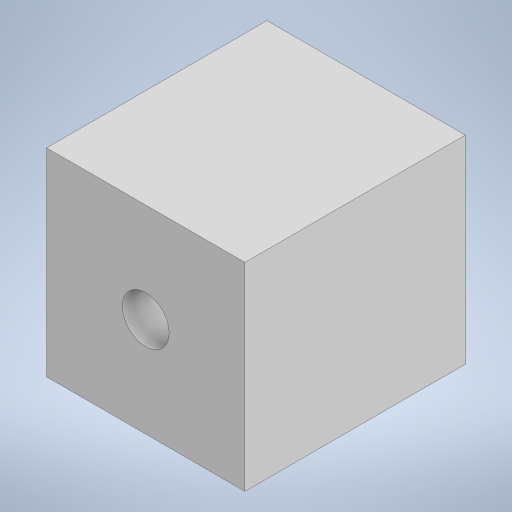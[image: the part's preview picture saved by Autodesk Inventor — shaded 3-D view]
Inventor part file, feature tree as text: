
AUTODESK INVENTOR PART (.ipt)
format: ipt  version: 2024 (Build 280153000, 153)  size: 172,032 bytes
history: native  units: mm
features: extrude x2, sketch x2
ambient origin geometry x8: Origin, YZ Plane, XZ Plane, XY Plane, X Axis, Y Axis, Z Axis, Center Point
bodies: Volumenkörper1 (feature_tree)
feature tree (4):
  extrude  "Extrusion1"  Depth=42.3mm
  extrude  "Extrusion2"  Depth=10.0mm
  sketch  "Skizze1"  dims[d0=42.3mm d1=42.3mm]
  sketch  "Skizze2"  dims[d2=47.0mm d3=0.0mm d4=10.0mm d5=47.0mm d6=0.0mm]
